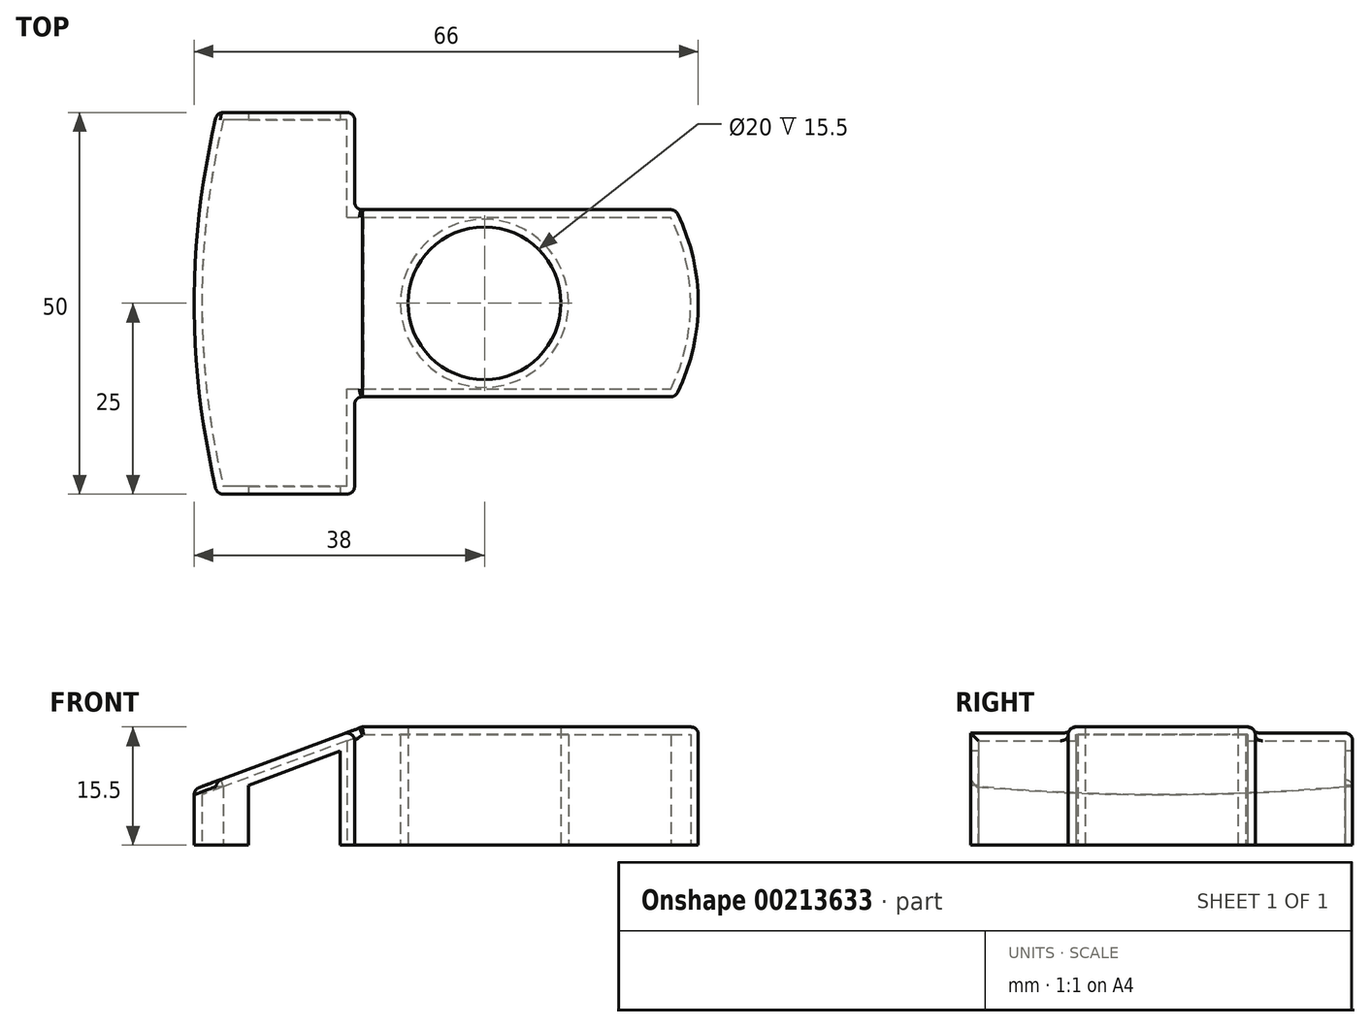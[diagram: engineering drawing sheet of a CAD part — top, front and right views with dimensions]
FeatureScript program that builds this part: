
annotation { "Feature Type Name" : "Feature", "Feature Type Description" : "" }
export const myFeature = defineFeature(function(context is Context, id is Id, definition is map)
    precondition{}
    {
        {
            var Q0;
            Q0=qCreatedBy(makeId("Top.planeOp"),FACE);
            var sketch = newSketch(context, id + "F0", { "sketchPlane" : qUnion([Q0])});
            skCircle(sketch, "E0", {"center": v(-4, 0) * mm, "radius": 10 * mm});
            skLineSegment(sketch, "E1.bottom", {"start": v(-21, -12.25) * mm, "end": v(21, -12.25) * mm});
            skLineSegment(sketch, "E1.top", {"start": v(-21, 12.25) * mm, "end": v(21, 12.25) * mm});
            skLineSegment(sketch, "E1.right", {"start": v(21, -12.25) * mm, "end": v(21, 12.25) * mm});
            skLineSegment(sketch, "E2.bottom", {"start": v(-21, -25) * mm, "end": v(-39, -25) * mm});
            skLineSegment(sketch, "E2.top", {"start": v(-21, 25) * mm, "end": v(-39, 25) * mm});
            skLineSegment(sketch, "E2.left", {"start": v(-21, -25) * mm, "end": v(-21, -12.25) * mm});
            skLineSegment(sketch, "E2.right", {"start": v(-39, -25) * mm, "end": v(-39, 25) * mm});
            skPoint(sketch, "E2.middle", {"position": v(-30, 0) * mm});
            skLineSegment(sketch, "E3.trimOffspring", {"start": v(-21, 12.25) * mm, "end": v(-21, 25) * mm});
            skLineSegment(sketch, "E4", {"start": v(-20, 12.25) * mm, "end": v(-20, -12.25) * mm});
            skArc(sketch, "E5", {"start": v(-39, 25) * mm, "mid": v(-42, 0) * mm, "end": v(-39, -25) * mm});
            skArc(sketch, "E6", {"start": v(21, -12.25) * mm, "mid": v(24, 0) * mm, "end": v(21, 12.25) * mm});
            skSolve(sketch);
        }
        {
            var Q0;
            Q0=qSketchRegion(id+"F0",true);
            extrude(context, id + "F1", {"entities" : qUnion([Q0]), "depth" : 15.5 * mm});
        }
        {
            var Q0;
            Q0=makeQuery(id+"F1.opExtrude","SWEPT_FACE",FACE,{"disambiguationData":[OSD([sQuery(id+"F0.wireOp",EDGE,"E2.bottom")])]});
            var sketch = newSketch(context, id + "F2", { "sketchPlane" : qUnion([Q0])});
            skLineSegment(sketch, "E7", {"start": v(-20, 15.5) * mm, "end": v(-42, 7.32) * mm});
            skLineSegment(sketch, "E8", {"start": v(-42, 7.32) * mm, "end": v(-42, 15.5) * mm});
            skLineSegment(sketch, "E9", {"start": v(-42, 15.5) * mm, "end": v(-20, 15.5) * mm});
            skSolve(sketch);
        }
        {
            var Q0;
            {var subQ0=sQuery(id+"F2.wireOp",EDGE,"E7");var subQ1=sQuery(id+"F0.wireOp",EDGE,"E2.bottom");var subQ2=makeQuery(id+"F1.opExtrude","SWEPT_EDGE",EDGE,{"disambiguationData":[OSD([subQ1,sQuery(id+"F0.wireOp",EDGE,"E2.left")])]});var subQ3=makeQuery(id+"F2.imprint","INTERSECT",VERTEX,{"derivedFrom":[subQ2,subQ0]});Q0=makeQuery(id+"F2.imprint","IMPRINT",FACE,{"disambiguationData":[TD([[makeQuery(id+"F2.imprint","IMPRINT",EDGE,{"disambiguationData":[TD([[subQ3,-1.0]])],"derivedFrom":subQ0}),-1.0]])]});}
            var Q1;
            {var subQ0=sQuery(id+"F2.wireOp",EDGE,"E8");Q1=makeQuery(id+"F2.imprint","IMPRINT",FACE,{"disambiguationData":[TD([[makeQuery(id+"F2.imprint","IMPRINT",EDGE,{"derivedFrom":subQ0}),-1.0]])]});}
            var Q2;
            {var subQ0=sQuery(id+"F2.wireOp",EDGE,"E9");var subQ1=sQuery(id+"F2.wireOp",EDGE,"E7");var subQ2=makeQuery(id+"F2.imprint","INTERSECT",VERTEX,{"derivedFrom":[subQ1,subQ0]});Q2=makeQuery(id+"F2.imprint","IMPRINT",FACE,{"disambiguationData":[TD([[makeQuery(id+"F2.imprint","IMPRINT",EDGE,{"disambiguationData":[TD([[subQ2,-1.0]])],"derivedFrom":subQ1}),-1.0]])]});}
            extrude(context, id + "F3", {"entities" : qUnion([Q0, Q1, Q2]), "operationType" : NewBodyOperationType.REMOVE, "endBound" : BoundingType.THROUGH_ALL, "oppositeDirection" : true, "depth" : 25 * mm});
        }
        {
            var Q0;
            {var subQ0=sQuery(id+"F0.wireOp",EDGE,"E1.right");var subQ1=sQuery(id+"F0.wireOp",EDGE,"E1.top");var subQ2=sQuery(id+"F0.wireOp",EDGE,"E1.bottom");var subQ3=sQuery(id+"F0.wireOp",EDGE,"E3.trimOffspring");var subQ4=sQuery(id+"F0.wireOp",EDGE,"E0");var subQ5=sQuery(id+"F0.wireOp",EDGE,"E2.bottom");var subQ6=sQuery(id+"F0.wireOp",EDGE,"E2.top");var subQ7=sQuery(id+"F0.wireOp",EDGE,"E2.left");Q0=makeQuery(id+"F6.boolean.opBoolean","SPLIT",FACE,{"disambiguationData":[TD([makeQuery(id+"F1.opExtrude","SWEPT_FACE",FACE,{"disambiguationData":[OSD([subQ4])]})])],"derivedFrom":makeQuery(id+"F1.opExtrude","CAP_FACE",FACE,{"disambiguationData":[OSD([subQ4,subQ2,subQ1,subQ0,subQ5,subQ6,subQ7,sQuery(id+"F0.wireOp",EDGE,"E2.right"),subQ3])],"isStart":true})});}
            shell(context, id + "F4", {"entities" : qUnion([Q0]), "thickness" : 1 * mm});
        }
        {
            var Q0;
            Q0=makeQuery(id+"F1.opExtrude","SWEPT_FACE",FACE,{"disambiguationData":[OSD([sQuery(id+"F0.wireOp",EDGE,"E2.bottom")])]});
            var sketch = newSketch(context, id + "F5", { "sketchPlane" : qUnion([Q0])});
            skLineSegment(sketch, "E10", {"start": v(-20, 15.5) * mm, "end": v(-39, 8.43) * mm});
            skLineSegment(sketch, "E11", {"start": v(-39, 8.43) * mm, "end": v(-39, 15.5) * mm});
            skLineSegment(sketch, "E12", {"start": v(-39, 15.5) * mm, "end": v(-20, 15.5) * mm});
            skLineSegment(sketch, "E13", {"start": v(-34.87, 0) * mm, "end": v(-34.87, 7.86) * mm});
            skLineSegment(sketch, "E14", {"start": v(-34.87, 7.86) * mm, "end": v(-22.87, 12.32) * mm});
            skLineSegment(sketch, "E15", {"start": v(-22.87, 0) * mm, "end": v(-34.87, 0) * mm});
            skLineSegment(sketch, "E16", {"start": v(-22.87, 12.32) * mm, "end": v(-22.87, 0) * mm});
            skSolve(sketch);
        }
        {
            var Q0;
            Q0=makeQuery(id+"F5.imprint","IMPRINT",FACE,{"disambiguationData":[TD([[makeQuery(id+"F5.imprint","IMPRINT",EDGE,{"derivedFrom":sQuery(id+"F5.wireOp",EDGE,"E13")}),-1.0]])]});
            extrude(context, id + "F6", {"entities" : qUnion([Q0]), "operationType" : NewBodyOperationType.REMOVE, "endBound" : BoundingType.THROUGH_ALL, "oppositeDirection" : true, "depth" : 25 * mm});
        }
        {
            var Q0;
            Q0=makeQuery(id+"F3.boolean.opBoolean","INTERSECT",EDGE,{"derivedFrom":[makeQuery(id+"F1.opExtrude","SWEPT_FACE",FACE,{"disambiguationData":[OSD([sQuery(id+"F0.wireOp",EDGE,"E2.left")])]}),makeQuery(id+"F3.opExtrude","SWEPT_FACE",FACE,{"disambiguationData":[OSD([sQuery(id+"F2.wireOp",EDGE,"E7")])]})]});
            var Q1;
            Q1=makeQuery(id+"F1.opExtrude","CAP_EDGE",EDGE,{"disambiguationData":[OSD([sQuery(id+"F0.wireOp",EDGE,"E1.bottom")])],"isStart":false});
            var Q2;
            Q2=makeQuery(id+"F3.boolean.opBoolean","INTERSECT",EDGE,{"derivedFrom":[makeQuery(id+"F1.opExtrude","SWEPT_FACE",FACE,{"disambiguationData":[OSD([sQuery(id+"F0.wireOp",EDGE,"E1.bottom")])]}),makeQuery(id+"F3.opExtrude","SWEPT_FACE",FACE,{"disambiguationData":[OSD([sQuery(id+"F2.wireOp",EDGE,"E7")])]})]});
            var Q3;
            Q3=makeQuery(id+"F3.boolean.opBoolean","INTERSECT",EDGE,{"derivedFrom":[makeQuery(id+"F1.opExtrude","SWEPT_FACE",FACE,{"disambiguationData":[OSD([sQuery(id+"F0.wireOp",EDGE,"E5")])]}),makeQuery(id+"F3.opExtrude","SWEPT_FACE",FACE,{"disambiguationData":[OSD([sQuery(id+"F2.wireOp",EDGE,"E7")])]})]});
            var Q4;
            Q4=makeQuery(id+"F3.boolean.opBoolean","INTERSECT",EDGE,{"derivedFrom":[makeQuery(id+"F1.opExtrude","SWEPT_FACE",FACE,{"disambiguationData":[OSD([sQuery(id+"F0.wireOp",EDGE,"E3.trimOffspring")])]}),makeQuery(id+"F3.opExtrude","SWEPT_FACE",FACE,{"disambiguationData":[OSD([sQuery(id+"F2.wireOp",EDGE,"E7")])]})]});
            var Q5;
            Q5=makeQuery(id+"F3.boolean.opBoolean","INTERSECT",EDGE,{"derivedFrom":[makeQuery(id+"F1.opExtrude","SWEPT_FACE",FACE,{"disambiguationData":[OSD([sQuery(id+"F0.wireOp",EDGE,"E1.top")])]}),makeQuery(id+"F3.opExtrude","SWEPT_FACE",FACE,{"disambiguationData":[OSD([sQuery(id+"F2.wireOp",EDGE,"E7")])]})]});
            var Q6;
            Q6=makeQuery(id+"F1.opExtrude","CAP_EDGE",EDGE,{"disambiguationData":[OSD([sQuery(id+"F0.wireOp",EDGE,"E1.top")])],"isStart":false});
            var Q7;
            Q7=makeQuery(id+"F1.opExtrude","CAP_EDGE",EDGE,{"disambiguationData":[OSD([sQuery(id+"F0.wireOp",EDGE,"E1.right")])],"isStart":false});
            var Q8;
            Q8=makeQuery(id+"F1.opExtrude","SWEPT_EDGE",EDGE,{"disambiguationData":[OSD([sQuery(id+"F0.wireOp",EDGE,"E1.bottom"),sQuery(id+"F0.wireOp",EDGE,"E1.right")])]});
            var Q9;
            Q9=makeQuery(id+"F1.opExtrude","SWEPT_EDGE",EDGE,{"disambiguationData":[OSD([sQuery(id+"F0.wireOp",EDGE,"E2.bottom"),sQuery(id+"F0.wireOp",EDGE,"E2.right"),sQuery(id+"F0.wireOp",EDGE,"E5")])]});
            var Q10;
            Q10=makeQuery(id+"F1.opExtrude","SWEPT_EDGE",EDGE,{"disambiguationData":[OSD([sQuery(id+"F0.wireOp",EDGE,"E2.bottom"),sQuery(id+"F0.wireOp",EDGE,"E2.left")])]});
            var Q11;
            Q11=makeQuery(id+"F1.opExtrude","SWEPT_EDGE",EDGE,{"disambiguationData":[OSD([sQuery(id+"F0.wireOp",EDGE,"E1.bottom"),sQuery(id+"F0.wireOp",EDGE,"E2.left")])]});
            var Q12;
            Q12=makeQuery(id+"F1.opExtrude","SWEPT_EDGE",EDGE,{"disambiguationData":[OSD([sQuery(id+"F0.wireOp",EDGE,"E1.top"),sQuery(id+"F0.wireOp",EDGE,"E1.right")])]});
            var Q13;
            Q13=makeQuery(id+"F1.opExtrude","SWEPT_EDGE",EDGE,{"disambiguationData":[OSD([sQuery(id+"F0.wireOp",EDGE,"E1.top"),sQuery(id+"F0.wireOp",EDGE,"E3.trimOffspring")])]});
            var Q14;
            Q14=makeQuery(id+"F1.opExtrude","SWEPT_EDGE",EDGE,{"disambiguationData":[OSD([sQuery(id+"F0.wireOp",EDGE,"E2.top"),sQuery(id+"F0.wireOp",EDGE,"E3.trimOffspring")])]});
            var Q15;
            Q15=makeQuery(id+"F3.boolean.opBoolean","INTERSECT",EDGE,{"derivedFrom":[makeQuery(id+"F1.opExtrude","SWEPT_FACE",FACE,{"disambiguationData":[OSD([sQuery(id+"F0.wireOp",EDGE,"E2.top")])]}),makeQuery(id+"F3.opExtrude","SWEPT_FACE",FACE,{"disambiguationData":[OSD([sQuery(id+"F2.wireOp",EDGE,"E7")])]})]});
            var Q16;
            Q16=makeQuery(id+"F1.opExtrude","SWEPT_EDGE",EDGE,{"disambiguationData":[OSD([sQuery(id+"F0.wireOp",EDGE,"E2.top"),sQuery(id+"F0.wireOp",EDGE,"E2.right"),sQuery(id+"F0.wireOp",EDGE,"E5")])]});
            var Q17;
            Q17=makeQuery(id+"F1.opExtrude","CAP_EDGE",EDGE,{"disambiguationData":[OSD([sQuery(id+"F0.wireOp",EDGE,"E6")])],"isStart":false});
            fillet(context, id + "F7", {"entities" : qUnion([Q0, Q1, Q2, Q3, Q4, Q5, Q6, Q7, Q8, Q9, Q10, Q11, Q12, Q13, Q14, Q15, Q16, Q17]), "radius" : 1 * mm, "tangentPropagation" : true, "allowEdgeOverflow" : false});
        }
    });
